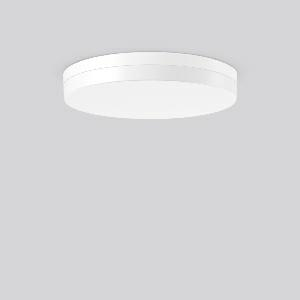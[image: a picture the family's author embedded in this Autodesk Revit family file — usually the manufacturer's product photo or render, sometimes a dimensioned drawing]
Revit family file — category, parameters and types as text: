
# Revit family: flat_slim_round_312634_002_5ffc
name_source: partatom
category: Lighting Fixtures
units: mm (PartAtom-declared; Revit-internal decimal feet)

## family parameters
Cut with Voids When Loaded = No
Host = Face
Light Source = No
Part Type = Normal
Room Calculation Point = No
Round Connector Dimension = Use Diameter
Shared = No

## types (1)
- MultiLumen 1 830 (1 x LED Modul 830, 3450 lm, 3000)
    Apparent Load = 26 VA
    CIE Flux Codes = 40 71 90 84 100
    Color Rendering = 80
    Color Temperature = 3000
    Default Elevation = 1800 mm
    Height = 70 mm
    Lamp = 1 x LED Modul 830
    Lamp Light Flux = 3450 lm
    Lamp count = 1
    Length = 480 mm
    Lifetime = 50000 h
    Luminous efficacy = 133 lm/W
    Manufacturer = RZB
    ModVariant = No
    Model = 312634.002
    Mounting Place = Ceiling
    Mounting Type = Surface mounted
    Number of Poles = 1
    OnlyDefault = Yes
    Power Factor = 1
    Product Name = FLAT SLIM round
    Product group = Surface mounted ceiling and wall luminaires
    ProductGroupID = 305
    Protection Class = Protection class I
    Protection Degree = Degree of protection
    RLX_Detail_Level = 1
    RLX_Emergency_Light_Flux = 0 lm
    RLX_Emergency_Type = 0
    RLX_Emergency_Type_DB = No
    RlxData = <blob elided: 21121 chars, md5=22347bc2>
    Socket = socket
    Standby Power = 0 W
    System Light Flux = 3450 lm
    System Power = 26 W
    Type Comments = MultiLumen 1 830
    Type Image = 312633.002.jpg
    URL = http://relux.com
    VarID = multilumen_1_830
    Voltage = 0 V
    Weight = 0.00 kg
    Width = 0 mm  [stored 0 ft]

note: [stored X ft] marks values corroborated as IEEE doubles in the binary element streams (Revit-internal decimal feet)

## geometry (parser evidence)
native form markers: Blend x4, Sweep x12
no freeform markers — native parametric forms only
